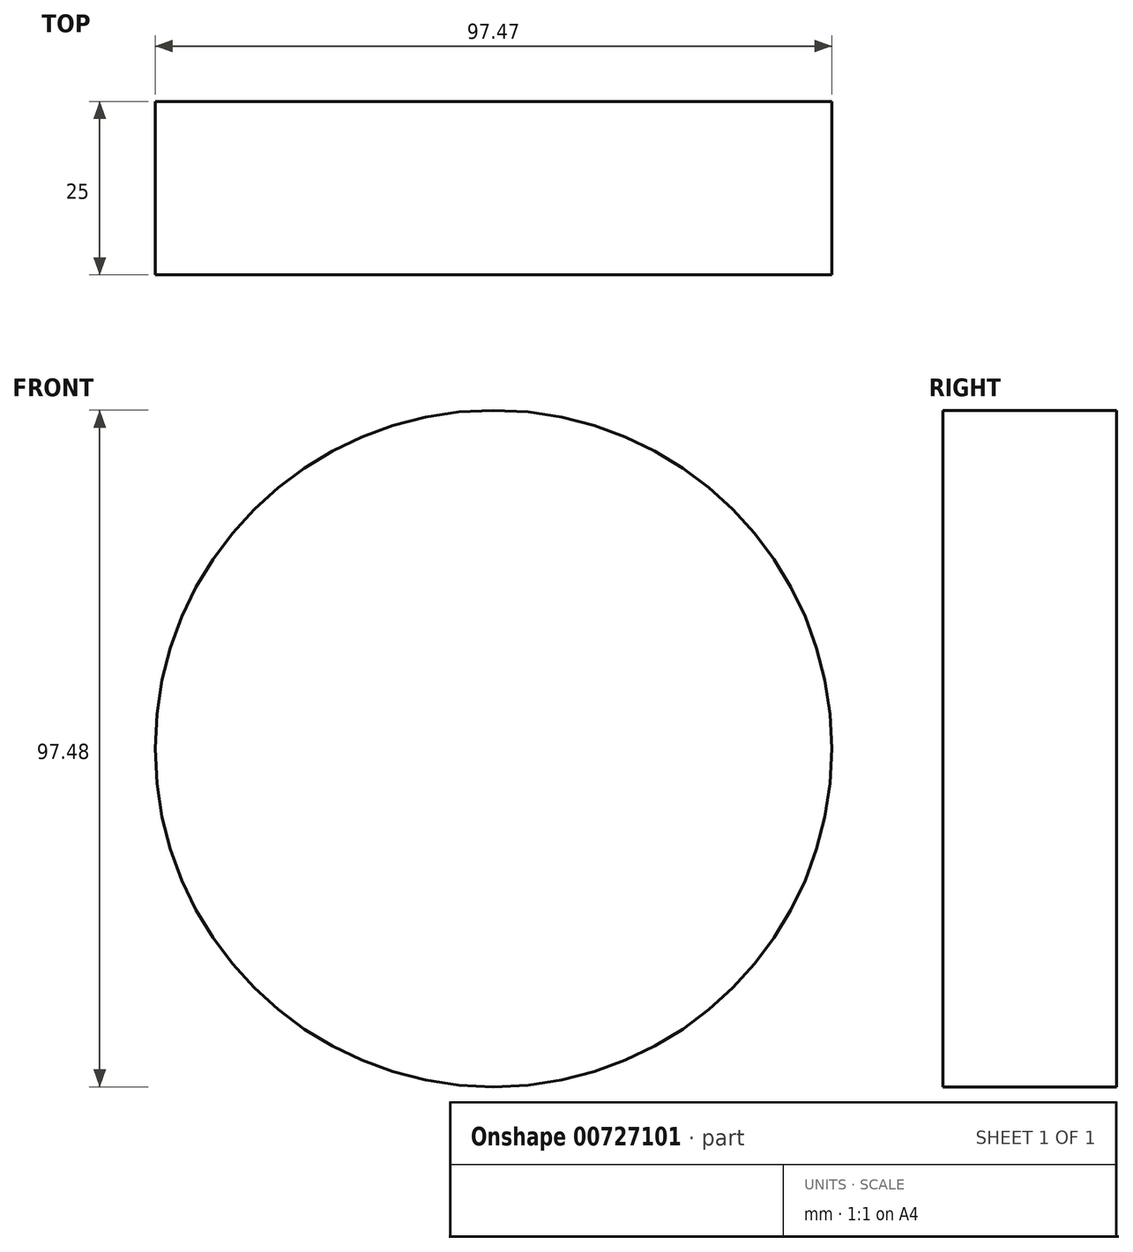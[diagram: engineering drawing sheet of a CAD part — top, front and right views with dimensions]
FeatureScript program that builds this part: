
annotation { "Feature Type Name" : "Feature", "Feature Type Description" : "" }
export const myFeature = defineFeature(function(context is Context, id is Id, definition is map)
    precondition{}
    {
        {
            var Q0;
            Q0=qCreatedBy(makeId("Front.planeOp"),FACE);
            var sketch = newSketch(context, id + "F0", { "sketchPlane" : qUnion([Q0])});
            skCircle(sketch, "E0", {"center": v(-23.48, 22.6) * mm, "radius": 48.74 * mm});
            skSolve(sketch);
        }
        {
            var Q0;
            Q0=makeQuery(id+"F0.imprint","IMPRINT",FACE,{"disambiguationData":[TD([[makeQuery(id+"F0.imprint","IMPRINT",EDGE,{"derivedFrom":sQuery(id+"F0.wireOp",EDGE,"E0")}),1.0]])]});
            extrude(context, id + "F1", {"entities" : qUnion([Q0]), "depth" : 25 * mm, "offsetDistance" : 25 * mm});
        }
    });
